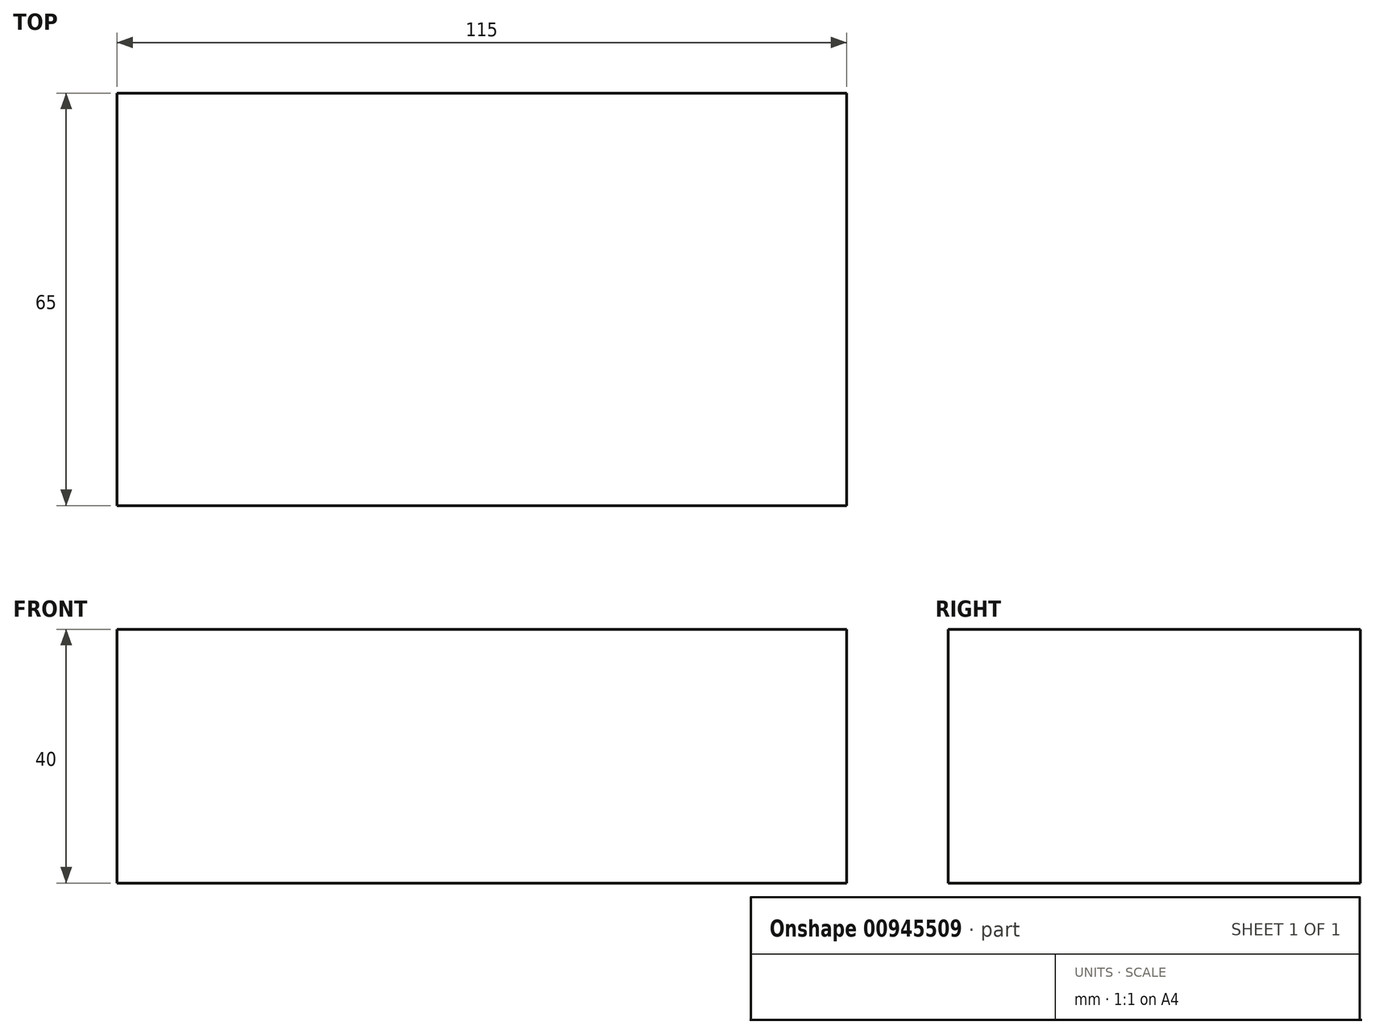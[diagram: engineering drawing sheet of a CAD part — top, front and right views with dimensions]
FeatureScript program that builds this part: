
annotation { "Feature Type Name" : "Feature", "Feature Type Description" : "" }
export const myFeature = defineFeature(function(context is Context, id is Id, definition is map)
    precondition{}
    {
        {
            var Q0;
            Q0=qCreatedBy(makeId("Front.planeOp"),FACE);
            var sketch = newSketch(context, id + "F0", { "sketchPlane" : qUnion([Q0])});
            skLineSegment(sketch, "E0.bottom", {"start": v(57.5, -20) * mm, "end": v(-57.5, -20) * mm});
            skLineSegment(sketch, "E0.top", {"start": v(57.5, 20) * mm, "end": v(-57.5, 20) * mm});
            skLineSegment(sketch, "E0.left", {"start": v(57.5, -20) * mm, "end": v(57.5, 20) * mm});
            skLineSegment(sketch, "E0.right", {"start": v(-57.5, -20) * mm, "end": v(-57.5, 20) * mm});
            skPoint(sketch, "E0.middle", {"position": v(0, 0) * mm});
            skSolve(sketch);
        }
        {
            var Q0;
            Q0=makeQuery(id+"F0.imprint","IMPRINT",FACE,{"disambiguationData":[TD([[makeQuery(id+"F0.imprint","IMPRINT",EDGE,{"derivedFrom":sQuery(id+"F0.wireOp",EDGE,"E0.bottom")}),-1.0]])]});
            extrude(context, id + "F1", {"entities" : qUnion([Q0]), "depth" : 65 * mm, "offsetDistance" : 25 * mm});
        }
    });
